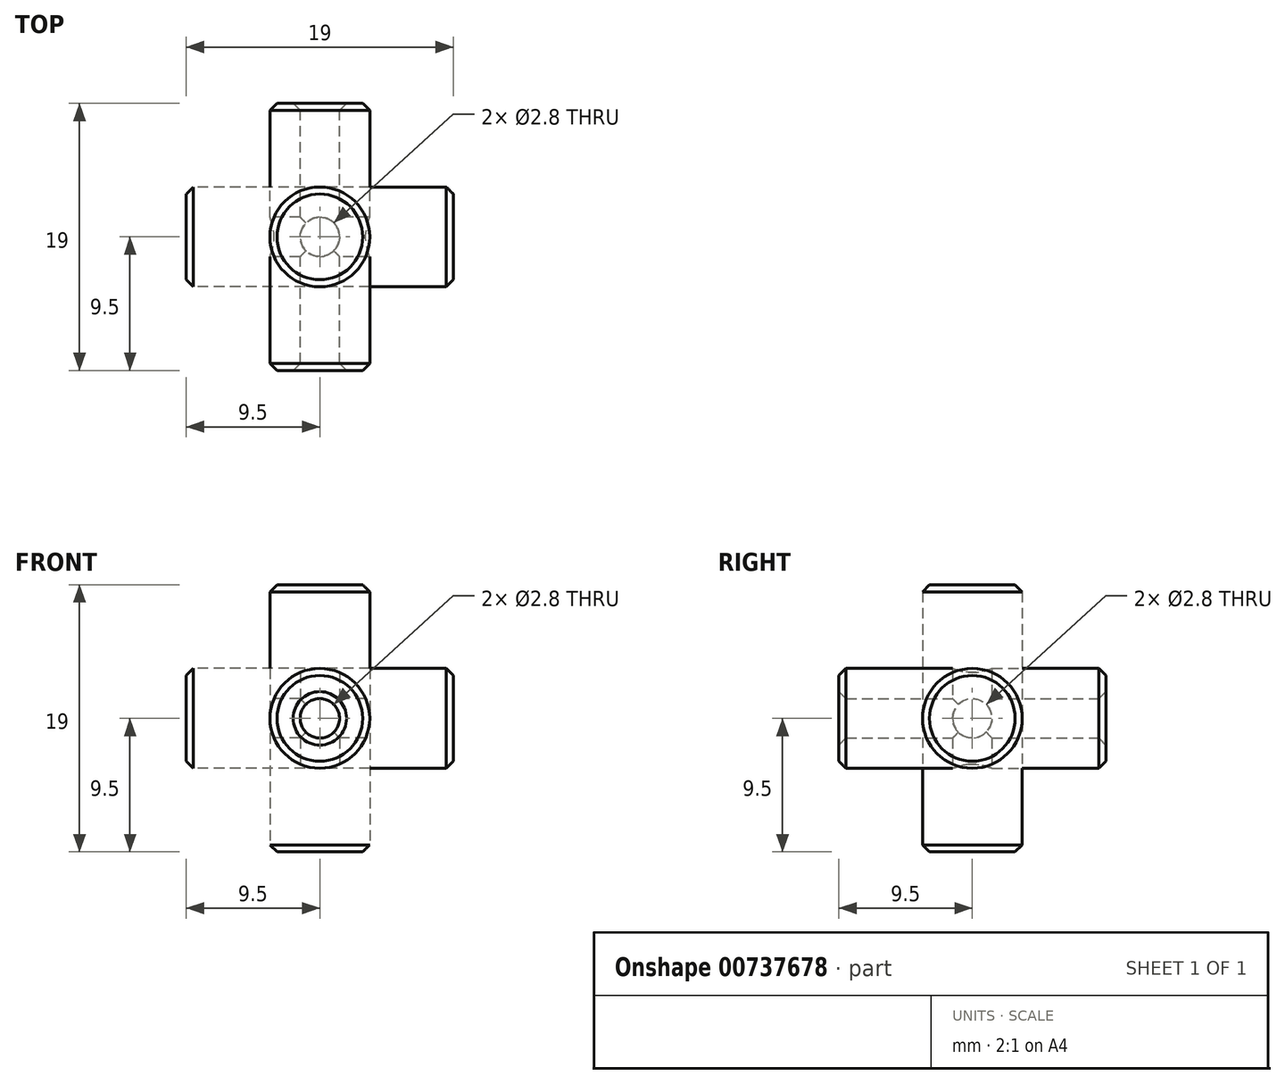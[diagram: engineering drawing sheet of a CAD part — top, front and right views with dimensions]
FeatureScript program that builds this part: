
annotation { "Feature Type Name" : "Feature", "Feature Type Description" : "" }
export const myFeature = defineFeature(function(context is Context, id is Id, definition is map)
    precondition{}
    {
        {
            var Q0;
            Q0=qCreatedBy(makeId("Front.planeOp"),FACE);
            var sketch = newSketch(context, id + "F0", { "sketchPlane" : qUnion([Q0])});
            skCircle(sketch, "E0", {"center": v(0, 0) * mm, "radius": 3.55 * mm});
            skSolve(sketch);
        }
        {
            var Q0;
            Q0=makeQuery(id+"F0.imprint","IMPRINT",FACE,{"disambiguationData":[TD([[makeQuery(id+"F0.imprint","IMPRINT",EDGE,{"derivedFrom":sQuery(id+"F0.wireOp",EDGE,"E0")}),1.0]])]});
            extrude(context, id + "F1", {"entities" : qUnion([Q0]), "endBound" : BoundingType.SYMMETRIC, "depth" : 19 * mm, "offsetDistance" : 25 * mm});
        }
        {
            var Q0;
            Q0=qCreatedBy(makeId("Front.planeOp"),FACE);
            var sketch = newSketch(context, id + "F2", { "sketchPlane" : qUnion([Q0])});
            skLineSegment(sketch, "E1.bottom", {"start": v(0, 0) * mm, "end": v(10, 0) * mm});
            skLineSegment(sketch, "E1.top", {"start": v(0, 10) * mm, "end": v(10, 10) * mm});
            skLineSegment(sketch, "E1.left", {"start": v(0, 0) * mm, "end": v(0, 10) * mm});
            skLineSegment(sketch, "E1.right", {"start": v(10, 0) * mm, "end": v(10, 10) * mm});
            skSolve(sketch);
        }
        {
            var Q0;
            Q0=makeQuery(id+"F2.imprint","IMPRINT",FACE,{"disambiguationData":[TD([[makeQuery(id+"F2.imprint","IMPRINT",EDGE,{"derivedFrom":sQuery(id+"F2.wireOp",EDGE,"E1.bottom")}),1.0]])]});
            extrude(context, id + "F3", {"entities" : qUnion([Q0]), "depth" : 10 * mm, "offsetDistance" : 25 * mm});
        }
        {
            var Q0;
            Q0=makeQuery(id+"F3.opExtrude","CAP_VERTEX",VERTEX,{"disambiguationData":[OSD([sQuery(id+"F2.wireOp",EDGE,"E1.top"),sQuery(id+"F2.wireOp",EDGE,"E1.left")])],"isStart":true});
            var Q1;
            Q1=makeQuery(id+"F3.opExtrude","CAP_VERTEX",VERTEX,{"disambiguationData":[OSD([sQuery(id+"F2.wireOp",EDGE,"E1.top"),sQuery(id+"F2.wireOp",EDGE,"E1.right")])],"isStart":false});
            var Q2;
            Q2=makeQuery(id+"F3.opExtrude","CAP_VERTEX",VERTEX,{"disambiguationData":[OSD([sQuery(id+"F2.wireOp",EDGE,"E1.bottom"),sQuery(id+"F2.wireOp",EDGE,"E1.right")])],"isStart":false});
            cPlane(context, id + "F4", {"entities" : qUnion([Q0, Q1, Q2]), "cplaneType" : CPlaneType.THREE_POINT, "offset" : 25 * mm, "width" : 150 * mm, "height" : 150 * mm});
        }
        {
            var Q0;
            Q0=qCreatedBy(id+"F4.planeOp",FACE);
            var sketch = newSketch(context, id + "F5", { "sketchPlane" : qUnion([Q0])});
            skLineSegment(sketch, "E2", {"start": v(0, 0) * mm, "end": v(14.14, 10) * mm});
            skSolve(sketch);
        }
        {
            var Q0;
            Q0=makeQuery(id+"F1.opExtrude","SWEPT_BODY",BODY,{"disambiguationData":[OSD([sQuery(id+"F0.wireOp",EDGE,"E0")])]});
            var Q1;
            Q1=sQuery(id+"F5.wireOp",EDGE,"E2");
            circularPattern(context, id + "F6", {"entities" : qUnion([Q0]), "axis" : qUnion([Q1]), "angle" : 360 * degree, "instanceCount" : 3, "equalSpace" : true});
        }
        {
            var Q0;
            Q0=makeQuery(id+"F3.opExtrude","SWEPT_BODY",BODY,{"disambiguationData":[OSD([sQuery(id+"F2.wireOp",EDGE,"E1.bottom"),sQuery(id+"F2.wireOp",EDGE,"E1.top"),sQuery(id+"F2.wireOp",EDGE,"E1.left"),sQuery(id+"F2.wireOp",EDGE,"E1.right")])]});
            deleteBodies(context, id + "F7", {"entities" : qUnion([Q0])});
        }
        {
            var Q0;
            Q0=qCreatedBy(makeId("Front.planeOp"),FACE);
            var sketch = newSketch(context, id + "F8", { "sketchPlane" : qUnion([Q0])});
            skCircle(sketch, "E3", {"center": v(0, 0) * mm, "radius": 1.4 * mm});
            skSolve(sketch);
        }
        {
            var Q0;
            Q0 = qSketchRegion(id + "F8", true);
            extrude(context, id + "F9", {"entities" : qUnion([Q0]), "endBound" : BoundingType.SYMMETRIC, "depth" : 25 * mm, "offsetDistance" : 25 * mm});
        }
        {
            var Q0;
            Q0=makeQuery(id+"F9.opExtrude","SWEPT_BODY",BODY,{"disambiguationData":[OSD([sQuery(id+"F8.wireOp",EDGE,"E3")])]});
            var Q1;
            Q1=sQuery(id+"F5.wireOp",EDGE,"E2");
            circularPattern(context, id + "F10", {"entities" : qUnion([Q0]), "axis" : qUnion([Q1]), "angle" : 360 * degree, "instanceCount" : 3, "equalSpace" : true});
        }
        {
            var Q0;
            Q0=makeQuery(id+"F10.opPattern","COPY",BODY,{"derivedFrom":makeQuery(id+"F9.opExtrude","SWEPT_BODY",BODY,{"disambiguationData":[OSD([sQuery(id+"F8.wireOp",EDGE,"E3")])]}),"instanceName":"1"});
            var Q1;
            Q1=makeQuery(id+"F9.opExtrude","SWEPT_BODY",BODY,{"disambiguationData":[OSD([sQuery(id+"F8.wireOp",EDGE,"E3")])]});
            var Q2;
            Q2=makeQuery(id+"F10.opPattern","COPY",BODY,{"derivedFrom":makeQuery(id+"F9.opExtrude","SWEPT_BODY",BODY,{"disambiguationData":[OSD([sQuery(id+"F8.wireOp",EDGE,"E3")])]}),"instanceName":"2"});
            var Q3;
            Q3=makeQuery(id+"F1.opExtrude","SWEPT_BODY",BODY,{"disambiguationData":[OSD([sQuery(id+"F0.wireOp",EDGE,"E0")])]});
            booleanBodies(context, id + "F11", {"operationType" : BooleanOperationType.SUBTRACTION, "tools" : qUnion([Q0, Q1, Q2]), "targets" : qUnion([Q3])});
        }
        {
            var Q0;
            Q0=makeQuery(id+"F6.opPattern","COPY",FACE,{"derivedFrom":makeQuery(id+"F1.opExtrude","CAP_FACE",FACE,{"disambiguationData":[OSD([sQuery(id+"F0.wireOp",EDGE,"E0")])],"isStart":false}),"instanceName":"1"});
            var Q1;
            Q1=makeQuery(id+"F6.opPattern","COPY",FACE,{"derivedFrom":makeQuery(id+"F1.opExtrude","CAP_FACE",FACE,{"disambiguationData":[OSD([sQuery(id+"F0.wireOp",EDGE,"E0")])],"isStart":false}),"instanceName":"2"});
            chamfer(context, id + "F12", {"entities" : qUnion([Q0, Q1]), "width" : 0.5 * mm, "tangentPropagation" : true});
        }
        {
            var Q0;
            Q0=makeQuery(id+"F1.opExtrude","CAP_FACE",FACE,{"disambiguationData":[OSD([sQuery(id+"F0.wireOp",EDGE,"E0")])],"isStart":true});
            var Q1;
            Q1=makeQuery(id+"F6.opPattern","COPY",FACE,{"derivedFrom":makeQuery(id+"F1.opExtrude","CAP_FACE",FACE,{"disambiguationData":[OSD([sQuery(id+"F0.wireOp",EDGE,"E0")])],"isStart":true}),"instanceName":"2"});
            chamfer(context, id + "F13", {"entities" : qUnion([Q0, Q1]), "width" : 0.5 * mm, "tangentPropagation" : true});
        }
        {
            var Q0;
            Q0=makeQuery(id+"F1.opExtrude","CAP_FACE",FACE,{"disambiguationData":[OSD([sQuery(id+"F0.wireOp",EDGE,"E0")])],"isStart":false});
            chamfer(context, id + "F14", {"entities" : qUnion([Q0]), "width" : 0.5 * mm, "tangentPropagation" : true});
        }
        {
            var Q0;
            Q0=makeQuery(id+"F6.opPattern","COPY",FACE,{"derivedFrom":makeQuery(id+"F1.opExtrude","CAP_FACE",FACE,{"disambiguationData":[OSD([sQuery(id+"F0.wireOp",EDGE,"E0")])],"isStart":true}),"instanceName":"1"});
            chamfer(context, id + "F15", {"entities" : qUnion([Q0]), "width" : 0.5 * mm, "tangentPropagation" : true});
        }
    });
